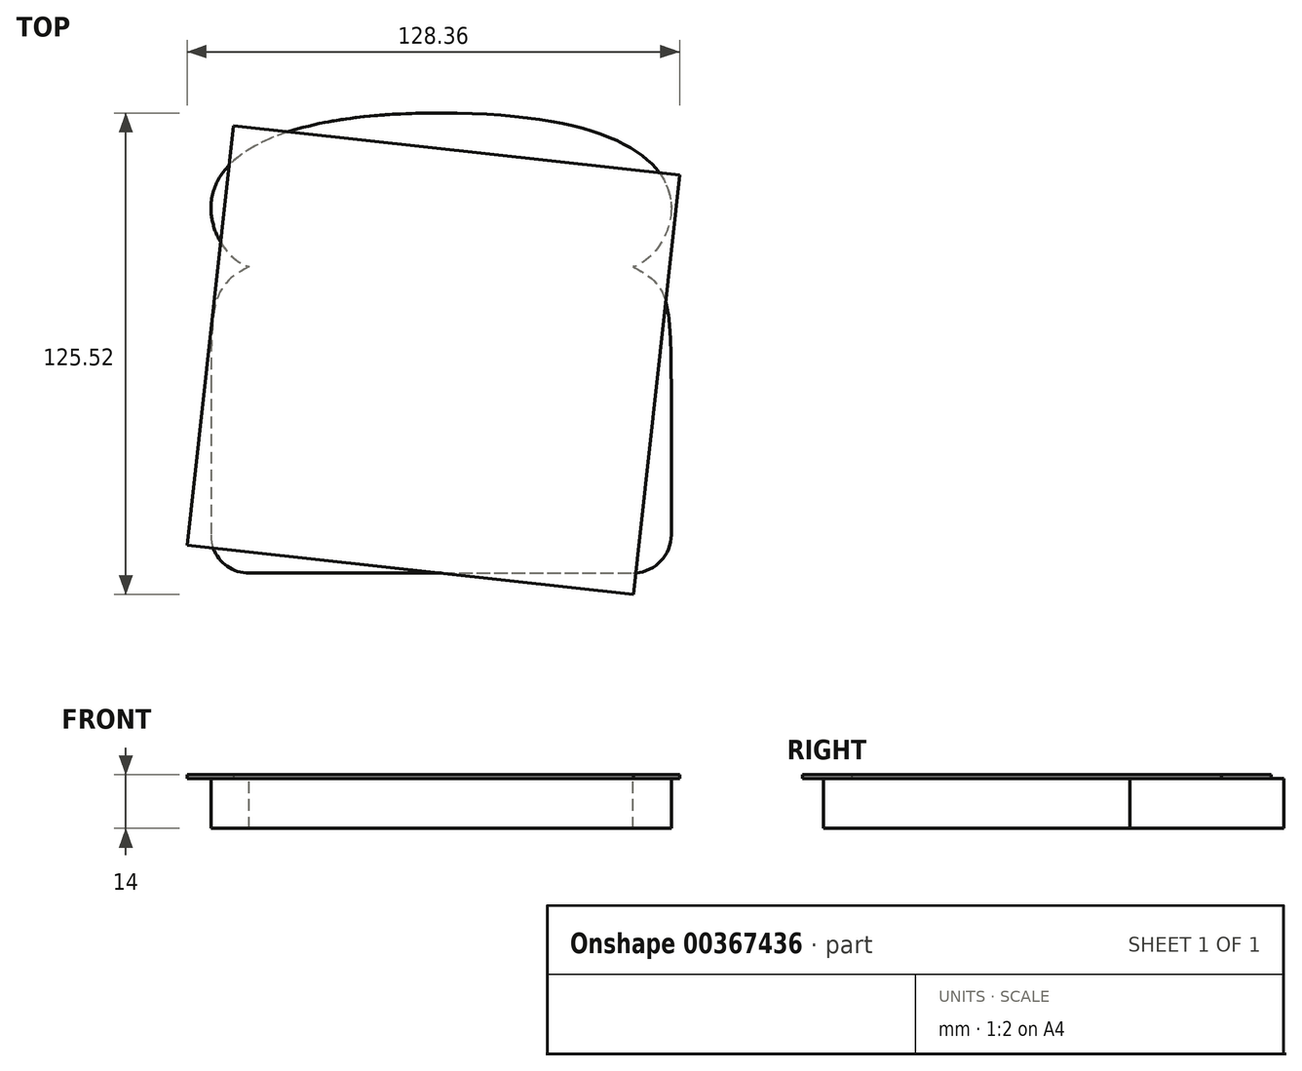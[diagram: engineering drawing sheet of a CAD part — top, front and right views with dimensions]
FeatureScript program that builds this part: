
annotation { "Feature Type Name" : "Feature", "Feature Type Description" : "" }
export const myFeature = defineFeature(function(context is Context, id is Id, definition is map)
    precondition{}
    {
        {
            var Q0;
            Q0=qCreatedBy(makeId("Top.planeOp"),FACE);
            var sketch = newSketch(context, id + "F0", { "sketchPlane" : qUnion([Q0])});
            skLineSegment(sketch, "E0", {"start": v(0, 81.07) * mm, "end": v(-60, 81.07) * mm});
            skLineSegment(sketch, "E1", {"start": v(-60, 81.07) * mm, "end": v(-60, -38.93) * mm});
            skLineSegment(sketch, "E2", {"start": v(-60, -38.93) * mm, "end": v(0, -38.93) * mm});
            skLineSegment(sketch, "E3.MirrorCS", {"start": v(60, -38.93) * mm, "end": v(0, -38.93) * mm});
            skLineSegment(sketch, "E4.MirrorCS", {"start": v(0, 81.07) * mm, "end": v(60, 81.07) * mm});
            skLineSegment(sketch, "E5.MirrorCS", {"start": v(60, 81.07) * mm, "end": v(60, -38.93) * mm});
            skSolve(sketch);
        }
        {
            var Q0;
            Q0=makeQuery(id+"F0.imprint","IMPRINT",FACE,{"disambiguationData":[TD([[makeQuery(id+"F0.imprint","IMPRINT",EDGE,{"derivedFrom":sQuery(id+"F0.wireOp",EDGE,"E0")}),1.0]])]});
            extrude(context, id + "F1", {"entities" : qUnion([Q0]), "depth" : 13 * mm});
        }
        {
            var Q0;
            Q0=makeQuery(id+"F1.opExtrude","CAP_FACE",FACE,{"disambiguationData":[OSD([sQuery(id+"F0.wireOp",EDGE,"E0"),sQuery(id+"F0.wireOp",EDGE,"E1"),sQuery(id+"F0.wireOp",EDGE,"E2"),sQuery(id+"F0.wireOp",EDGE,"E3.MirrorCS"),sQuery(id+"F0.wireOp",EDGE,"E4.MirrorCS"),sQuery(id+"F0.wireOp",EDGE,"E5.MirrorCS")])],"isStart":false});
            var sketch = newSketch(context, id + "F2", { "sketchPlane" : qUnion([Q0])});
            skFitSpline(sketch, "E6", {"points": [v(0, 81.07) * mm, v(-60, 56.24) * mm], "startDerivative": vector(-128.4, 0) * mm, "endDerivative": vector(0, -40.61) * mm});
            skFitSpline(sketch, "E7", {"points": [v(-60, 56.24) * mm, v(-50.07, 40.95) * mm], "startDerivative": vector(0, -19.56) * mm, "endDerivative": vector(16.38, -5.02) * mm});
            skFitSpline(sketch, "E8", {"points": [v(-50.07, 40.95) * mm, v(-60, 11.07) * mm], "startDerivative": vector(-25.68, -13.94) * mm, "endDerivative": vector(0, -69.08) * mm});
            skLineSegment(sketch, "E9", {"start": v(-60, 11.07) * mm, "end": v(-60, -28.93) * mm});
            skLineSegment(sketch, "E10", {"start": v(-50, -38.93) * mm, "end": v(0, -38.93) * mm});
            skPoint(sketch, "E11.visualSharp", {"position": v(-60, -38.93) * mm});
            skArc(sketch, "E11.filletArc", {"start": v(-60, -28.93) * mm, "mid": v(-57.07, -36) * mm, "end": v(-50, -38.93) * mm});
            skLineSegment(sketch, "E12", {"start": v(0, -38.93) * mm, "end": v(0, -77.2) * mm});
            skLineSegment(sketch, "E13", {"start": v(0, -77.2) * mm, "end": v(-101.8, -77.2) * mm});
            skLineSegment(sketch, "E14", {"start": v(-101.8, -77.2) * mm, "end": v(-101.8, 81.07) * mm});
            skLineSegment(sketch, "E15", {"start": v(0, 81.07) * mm, "end": v(0, 81.07) * mm});
            skArc(sketch, "E16.MirrorCS", {"start": v(60, -28.93) * mm, "mid": v(57.07, -36) * mm, "end": v(50, -38.93) * mm});
            skFitSpline(sketch, "E17.MirrorCS", {"points": [v(60, 56.24) * mm, v(50.07, 40.95) * mm], "startDerivative": vector(0, -19.56) * mm, "endDerivative": vector(-16.38, -5.02) * mm});
            skLineSegment(sketch, "E18.MirrorCS", {"start": v(0, -77.2) * mm, "end": v(101.8, -77.2) * mm});
            skLineSegment(sketch, "E19.MirrorCS", {"start": v(50, -38.93) * mm, "end": v(0, -38.93) * mm});
            skFitSpline(sketch, "E20.MirrorCS", {"points": [v(0, 81.07) * mm, v(60, 56.24) * mm], "startDerivative": vector(128.4, 0) * mm, "endDerivative": vector(0, -40.61) * mm});
            skLineSegment(sketch, "E21.MirrorCS", {"start": v(101.8, -77.2) * mm, "end": v(101.8, 81.07) * mm});
            skLineSegment(sketch, "E22.MirrorCS", {"start": v(60, 11.07) * mm, "end": v(60, -28.93) * mm});
            skPoint(sketch, "E23.MirrorP", {"position": v(60, -38.93) * mm});
            skFitSpline(sketch, "E24.MirrorCS", {"points": [v(50.07, 40.95) * mm, v(60, 11.07) * mm], "startDerivative": vector(25.68, -13.94) * mm, "endDerivative": vector(0, -69.08) * mm});
            skLineSegment(sketch, "E25", {"start": v(-101.8, 81.07) * mm, "end": v(-101.8, 114.12) * mm});
            skLineSegment(sketch, "E26", {"start": v(-101.8, 114.12) * mm, "end": v(101.8, 114.12) * mm});
            skLineSegment(sketch, "E27", {"start": v(101.8, 114.12) * mm, "end": v(101.8, 81.07) * mm});
            skSolve(sketch);
        }
        {
            var Q0;
            Q0 = qSketchRegion(id + "F2", true);
            extrude(context, id + "F3", {"entities" : qUnion([Q0]), "operationType" : NewBodyOperationType.REMOVE, "oppositeDirection" : true, "depth" : 25 * mm});
        }
        {
            var Q0;
            Q0=makeQuery(id+"F1.opExtrude","CAP_FACE",FACE,{"disambiguationData":[OSD([sQuery(id+"F0.wireOp",EDGE,"E0"),sQuery(id+"F0.wireOp",EDGE,"E1"),sQuery(id+"F0.wireOp",EDGE,"E2"),sQuery(id+"F0.wireOp",EDGE,"E3.MirrorCS"),sQuery(id+"F0.wireOp",EDGE,"E4.MirrorCS"),sQuery(id+"F0.wireOp",EDGE,"E5.MirrorCS")])],"isStart":false});
            var sketch = newSketch(context, id + "F4", { "sketchPlane" : qUnion([Q0])});
            skLineSegment(sketch, "E28", {"start": v(-54.12, 77.72) * mm, "end": v(62.18, 64.88) * mm});
            skLineSegment(sketch, "E29", {"start": v(62.18, 64.88) * mm, "end": v(50.11, -44.45) * mm});
            skLineSegment(sketch, "E30", {"start": v(50.11, -44.45) * mm, "end": v(-66.18, -31.62) * mm});
            skLineSegment(sketch, "E31", {"start": v(-66.18, -31.62) * mm, "end": v(-54.12, 77.72) * mm});
            skSolve(sketch);
        }
        {
            var Q0;
            Q0 = qSketchRegion(id + "F4", true);
            extrude(context, id + "F5", {"entities" : qUnion([Q0]), "operationType" : NewBodyOperationType.ADD, "depth" : 1 * mm});
        }
    });
